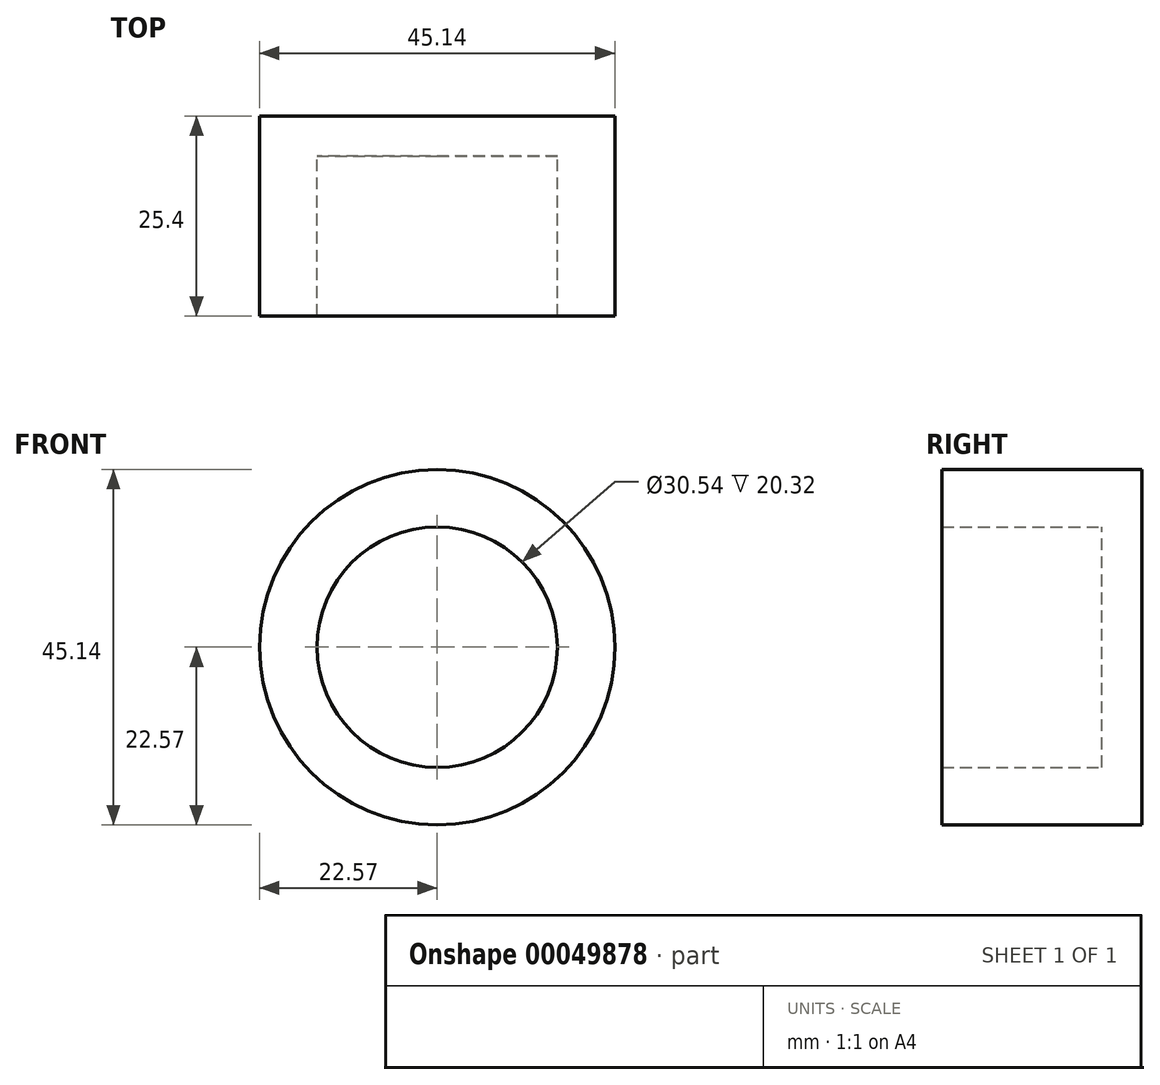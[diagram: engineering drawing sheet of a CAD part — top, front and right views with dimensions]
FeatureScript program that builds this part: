
annotation { "Feature Type Name" : "Feature", "Feature Type Description" : "" }
export const myFeature = defineFeature(function(context is Context, id is Id, definition is map)
    precondition{}
    {
        {
            var Q0;
            Q0=qCreatedBy(makeId("Front.planeOp"),FACE);
            var sketch = newSketch(context, id + "F0", { "sketchPlane" : qUnion([Q0])});
            skCircle(sketch, "E0", {"center": v(0, 0) * mm, "radius": 22.57 * mm});
            skCircle(sketch, "E1", {"center": v(0, 0) * mm, "radius": 15.27 * mm});
            skSolve(sketch);
        }
        {
            var Q0;
            Q0=makeQuery(id+"F0.imprint","IMPRINT",FACE,{"disambiguationData":[TD([[makeQuery(id+"F0.imprint","IMPRINT",EDGE,{"derivedFrom":sQuery(id+"F0.wireOp",EDGE,"E1")}),1.0]])]});
            extrude(context, id + "F1", {"entities" : qUnion([Q0]), "depth" : 5.08 * mm});
        }
        {
            var Q0;
            Q0=makeQuery(id+"F0.imprint","IMPRINT",FACE,{"disambiguationData":[TD([[makeQuery(id+"F0.imprint","IMPRINT",EDGE,{"derivedFrom":sQuery(id+"F0.wireOp",EDGE,"E0")}),1.0]])]});
            extrude(context, id + "F2", {"entities" : qUnion([Q0]), "operationType" : NewBodyOperationType.ADD, "depth" : 25.4 * mm});
        }
    });
